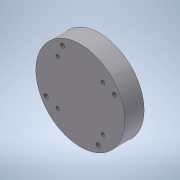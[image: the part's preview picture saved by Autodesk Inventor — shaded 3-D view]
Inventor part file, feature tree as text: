
AUTODESK INVENTOR PART (.ipt)
format: ipt  version: 2020.3 (Build 243373000, 373)  size: 142,336 bytes
history: native  units: in
note: dims shown in document units (in); Inventor stores cm internally (conversion verified against a paired STEP export)
features: sketch x3, hole x2, extrude x1, pattern_circular x1
ambient origin geometry x8: Origin, YZ Plane, XZ Plane, XY Plane, X Axis, Y Axis, Z Axis, Center Point
bodies: Solid1 (feature_tree)
feature tree (7):
  extrude  "Extrusion1"  Depth=3.75in
  hole  "Hole1"  [1 undecoded]
  hole  "Hole2"  [1 undecoded]
  pattern_circular  "Circular Pattern1"  [2 undecoded]
  sketch  "Sketch1"  dims[d0=0.8125in d1=3.75in]
  sketch  "Sketch2"  dims[d2=0.81in d3=0.0in]
  sketch  "Sketch3"  dims[d5=0.1628in d6=0.394in d7=0.375in d8=0.25in d9=0.5635in d10=0.559in d11=0.8108in d12=1.5748in d13=360.0deg d15=0.1936in d16=0.472in d17=0.375in d18=0.25in d19=0.5635in d20=0.673in d21=0.8108in d22=1.902in d23=3.25in d24=0.4295in d25=2.6898in]
note: 4 required parameter values undecoded (feature->parameter linkage not recoverable at this tier; creation-order binding heuristic only, values carry confidence <= 0.55)
